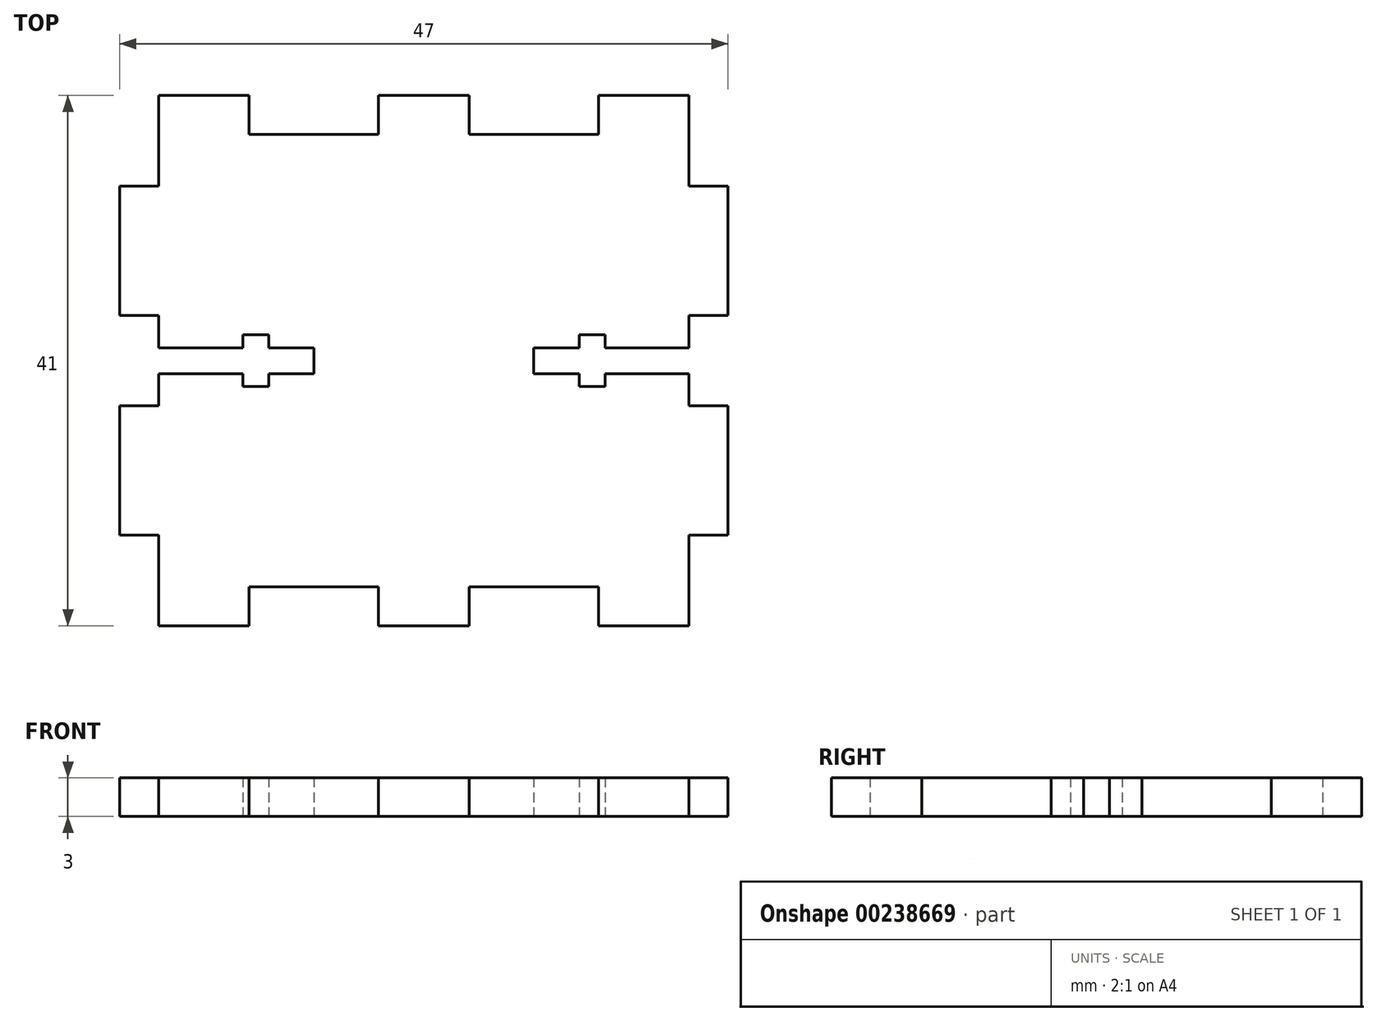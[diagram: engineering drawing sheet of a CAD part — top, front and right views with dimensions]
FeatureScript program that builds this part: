
annotation { "Feature Type Name" : "Feature", "Feature Type Description" : "" }
export const myFeature = defineFeature(function(context is Context, id is Id, definition is map)
    precondition{}
    {
        {
            var Q0;
            Q0=qCreatedBy(makeId("Top.planeOp"),FACE);
            var sketch = newSketch(context, id + "F0", { "sketchPlane" : qUnion([Q0])});
            skLineSegment(sketch, "E0", {"start": v(3.47, -20.5) * mm, "end": v(3.47, -17.5) * mm});
            skLineSegment(sketch, "E1", {"start": v(3.47, -17.5) * mm, "end": v(13.47, -17.5) * mm});
            skLineSegment(sketch, "E2", {"start": v(20.47, -13.5) * mm, "end": v(23.47, -13.5) * mm});
            skLineSegment(sketch, "E3", {"start": v(23.47, -13.5) * mm, "end": v(23.47, -3.5) * mm});
            skLineSegment(sketch, "E4", {"start": v(23.47, -3.5) * mm, "end": v(20.47, -3.5) * mm});
            skLineSegment(sketch, "E5", {"start": v(20.47, -3.5) * mm, "end": v(20.47, -1) * mm});
            skLineSegment(sketch, "E6", {"start": v(20.47, -1) * mm, "end": v(13.97, -1) * mm});
            skLineSegment(sketch, "E7", {"start": v(13.97, -1) * mm, "end": v(13.97, -2) * mm});
            skLineSegment(sketch, "E8", {"start": v(13.97, -2) * mm, "end": v(11.97, -2) * mm});
            skLineSegment(sketch, "E9", {"start": v(11.97, -2) * mm, "end": v(11.97, -1) * mm});
            skLineSegment(sketch, "E10", {"start": v(11.97, -1) * mm, "end": v(8.47, -1) * mm});
            skLineSegment(sketch, "E11", {"start": v(8.47, -1) * mm, "end": v(8.47, 0) * mm});
            skLineSegment(sketch, "E12", {"start": v(23.96, 0) * mm, "end": v(-20.53, 0) * mm, "construction": true});
            skLineSegment(sketch, "E13", {"start": v(-0.03, -20.5) * mm, "end": v(3.47, -20.5) * mm});
            skLineSegment(sketch, "E14", {"start": v(-0.03, 20.5) * mm, "end": v(-0.03, -20.5) * mm, "construction": true});
            skLineSegment(sketch, "E15", {"start": v(13.47, -17.5) * mm, "end": v(13.47, -20.5) * mm});
            skLineSegment(sketch, "E16", {"start": v(13.47, -20.5) * mm, "end": v(20.47, -20.5) * mm});
            skLineSegment(sketch, "E17", {"start": v(20.47, -20.5) * mm, "end": v(20.47, -13.5) * mm});
            skLineSegment(sketch, "E18.MirrorCS", {"start": v(13.97, 2) * mm, "end": v(11.97, 2) * mm});
            skLineSegment(sketch, "E19.MirrorCS", {"start": v(20.47, 13.5) * mm, "end": v(23.47, 13.5) * mm});
            skLineSegment(sketch, "E20.MirrorCS", {"start": v(8.47, 1) * mm, "end": v(8.47, 0) * mm});
            skLineSegment(sketch, "E21.MirrorCS", {"start": v(20.47, 3.5) * mm, "end": v(20.47, 1) * mm});
            skLineSegment(sketch, "E22.MirrorCS", {"start": v(11.97, 2) * mm, "end": v(11.97, 1) * mm});
            skLineSegment(sketch, "E23.MirrorCS", {"start": v(23.47, 3.5) * mm, "end": v(20.47, 3.5) * mm});
            skLineSegment(sketch, "E24.MirrorCS", {"start": v(13.97, 1) * mm, "end": v(13.97, 2) * mm});
            skLineSegment(sketch, "E25.MirrorCS", {"start": v(13.47, 20.5) * mm, "end": v(20.47, 20.5) * mm});
            skLineSegment(sketch, "E26.MirrorCS", {"start": v(20.47, 1) * mm, "end": v(13.97, 1) * mm});
            skLineSegment(sketch, "E27.MirrorCS", {"start": v(20.47, 20.5) * mm, "end": v(20.47, 13.5) * mm});
            skLineSegment(sketch, "E28.MirrorCS", {"start": v(11.97, 1) * mm, "end": v(8.47, 1) * mm});
            skLineSegment(sketch, "E29.MirrorCS", {"start": v(3.47, 20.5) * mm, "end": v(3.47, 17.5) * mm});
            skLineSegment(sketch, "E30.MirrorCS", {"start": v(3.47, 17.5) * mm, "end": v(13.47, 17.5) * mm});
            skLineSegment(sketch, "E31.MirrorCS", {"start": v(23.47, 13.5) * mm, "end": v(23.47, 3.5) * mm});
            skLineSegment(sketch, "E32.MirrorCS", {"start": v(-0.03, 20.5) * mm, "end": v(3.47, 20.5) * mm});
            skLineSegment(sketch, "E33.MirrorCS", {"start": v(13.47, 17.5) * mm, "end": v(13.47, 20.5) * mm});
            skLineSegment(sketch, "E34.MirrorCS", {"start": v(-8.53, 1) * mm, "end": v(-8.53, 0) * mm});
            skLineSegment(sketch, "E35.MirrorCS", {"start": v(-14.03, -1) * mm, "end": v(-14.03, -2) * mm});
            skLineSegment(sketch, "E36.MirrorCS", {"start": v(-8.53, -1) * mm, "end": v(-8.53, 0) * mm});
            skLineSegment(sketch, "E37.MirrorCS", {"start": v(-14.03, 2) * mm, "end": v(-12.03, 2) * mm});
            skLineSegment(sketch, "E38.MirrorCS", {"start": v(-14.03, 1) * mm, "end": v(-14.03, 2) * mm});
            skLineSegment(sketch, "E39.MirrorCS", {"start": v(-12.03, 1) * mm, "end": v(-8.53, 1) * mm});
            skLineSegment(sketch, "E40.MirrorCS", {"start": v(-12.03, -2) * mm, "end": v(-12.03, -1) * mm});
            skLineSegment(sketch, "E41.MirrorCS", {"start": v(-14.03, -2) * mm, "end": v(-12.03, -2) * mm});
            skLineSegment(sketch, "E42.MirrorCS", {"start": v(-12.03, -1) * mm, "end": v(-8.53, -1) * mm});
            skLineSegment(sketch, "E43.MirrorCS", {"start": v(-0.03, -20.5) * mm, "end": v(-3.53, -20.5) * mm});
            skLineSegment(sketch, "E44.MirrorCS", {"start": v(-13.53, -17.5) * mm, "end": v(-13.53, -20.5) * mm});
            skLineSegment(sketch, "E45.MirrorCS", {"start": v(-20.53, -13.5) * mm, "end": v(-23.53, -13.5) * mm});
            skLineSegment(sketch, "E46.MirrorCS", {"start": v(-20.53, -3.5) * mm, "end": v(-20.53, -1) * mm});
            skLineSegment(sketch, "E47.MirrorCS", {"start": v(-13.53, 17.5) * mm, "end": v(-13.53, 20.5) * mm});
            skLineSegment(sketch, "E48.MirrorCS", {"start": v(-12.03, 2) * mm, "end": v(-12.03, 1) * mm});
            skLineSegment(sketch, "E49.MirrorCS", {"start": v(-20.53, 13.5) * mm, "end": v(-23.53, 13.5) * mm});
            skLineSegment(sketch, "E50.MirrorCS", {"start": v(-3.53, -20.5) * mm, "end": v(-3.53, -17.5) * mm});
            skLineSegment(sketch, "E51.MirrorCS", {"start": v(-0.03, 20.5) * mm, "end": v(-3.53, 20.5) * mm});
            skLineSegment(sketch, "E52.MirrorCS", {"start": v(-3.53, 20.5) * mm, "end": v(-3.53, 17.5) * mm});
            skLineSegment(sketch, "E53.MirrorCS", {"start": v(-20.53, 3.5) * mm, "end": v(-20.53, 1) * mm});
            skLineSegment(sketch, "E54.MirrorCS", {"start": v(-23.53, 3.5) * mm, "end": v(-20.53, 3.5) * mm});
            skLineSegment(sketch, "E55.MirrorCS", {"start": v(-23.53, -3.5) * mm, "end": v(-20.53, -3.5) * mm});
            skLineSegment(sketch, "E56.MirrorCS", {"start": v(-23.53, 13.5) * mm, "end": v(-23.53, 3.5) * mm});
            skLineSegment(sketch, "E57.MirrorCS", {"start": v(-3.53, 17.5) * mm, "end": v(-13.53, 17.5) * mm});
            skLineSegment(sketch, "E58.MirrorCS", {"start": v(-13.53, 20.5) * mm, "end": v(-20.53, 20.5) * mm});
            skLineSegment(sketch, "E59.MirrorCS", {"start": v(-20.53, -1) * mm, "end": v(-14.03, -1) * mm});
            skLineSegment(sketch, "E60.MirrorCS", {"start": v(-20.53, 1) * mm, "end": v(-14.03, 1) * mm});
            skLineSegment(sketch, "E61.MirrorCS", {"start": v(-3.53, -17.5) * mm, "end": v(-13.53, -17.5) * mm});
            skLineSegment(sketch, "E62.MirrorCS", {"start": v(-20.53, -20.5) * mm, "end": v(-20.53, -13.5) * mm});
            skLineSegment(sketch, "E63.MirrorCS", {"start": v(-13.53, -20.5) * mm, "end": v(-20.53, -20.5) * mm});
            skLineSegment(sketch, "E64.MirrorCS", {"start": v(-20.53, 20.5) * mm, "end": v(-20.53, 13.5) * mm});
            skLineSegment(sketch, "E65.MirrorCS", {"start": v(-23.53, -13.5) * mm, "end": v(-23.53, -3.5) * mm});
            skSolve(sketch);
        }
        {
            var Q0;
            Q0=qSketchRegion(id+"F0",true);
            extrude(context, id + "F1", {"entities" : qUnion([Q0]), "depth" : 3 * mm});
        }
    });
